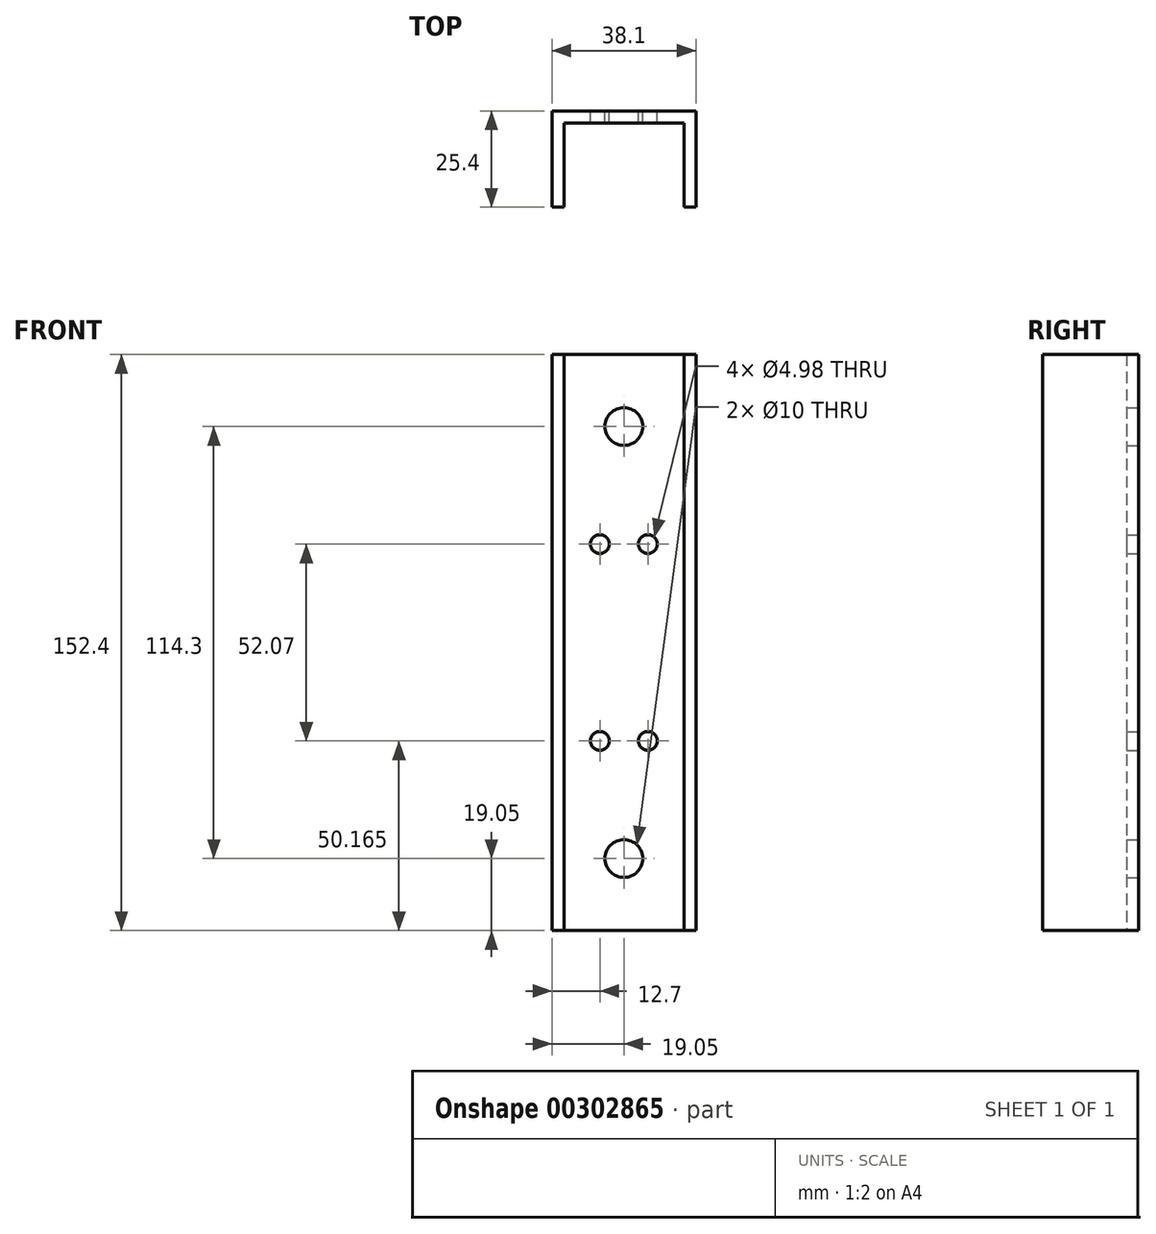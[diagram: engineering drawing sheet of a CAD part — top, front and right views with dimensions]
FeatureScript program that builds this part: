
annotation { "Feature Type Name" : "Feature", "Feature Type Description" : "" }
export const myFeature = defineFeature(function(context is Context, id is Id, definition is map)
    precondition{}
    {
        {
            var Q0;
            Q0=qCreatedBy(makeId("Top.planeOp"),FACE);
            var sketch = newSketch(context, id + "F0", { "sketchPlane" : qUnion([Q0])});
            skLineSegment(sketch, "E0", {"start": v(0, 0) * mm, "end": v(38.1, 0) * mm});
            skLineSegment(sketch, "E1", {"start": v(38.1, 0) * mm, "end": v(38.1, -25.4) * mm});
            skLineSegment(sketch, "E2", {"start": v(38.1, -25.4) * mm, "end": v(34.93, -25.4) * mm});
            skLineSegment(sketch, "E3", {"start": v(0, 0) * mm, "end": v(0, -25.4) * mm});
            skLineSegment(sketch, "E4", {"start": v(0, -25.4) * mm, "end": v(3.18, -25.4) * mm});
            skLineSegment(sketch, "E5", {"start": v(3.18, -25.4) * mm, "end": v(3.18, -3.18) * mm});
            skLineSegment(sketch, "E6", {"start": v(34.93, -25.4) * mm, "end": v(34.93, -3.18) * mm});
            skLineSegment(sketch, "E7", {"start": v(3.18, -3.18) * mm, "end": v(34.93, -3.18) * mm});
            skSolve(sketch);
        }
        {
            var Q0;
            Q0=makeQuery(id+"F0.imprint","IMPRINT",FACE,{"disambiguationData":[TD([[makeQuery(id+"F0.imprint","IMPRINT",EDGE,{"derivedFrom":sQuery(id+"F0.wireOp",EDGE,"E0")}),-1.0]])]});
            extrude(context, id + "F1", {"entities" : qUnion([Q0]), "depth" : 152.4 * mm});
        }
        {
            var Q0;
            Q0=makeQuery(id+"F1.opExtrude","SWEPT_FACE",FACE,{"disambiguationData":[OSD([sQuery(id+"F0.wireOp",EDGE,"E0")])]});
            var sketch = newSketch(context, id + "F2", { "sketchPlane" : qUnion([Q0])});
            skCircle(sketch, "E8", {"center": v(-19.05, 133.35) * mm, "radius": 5 * mm});
            skCircle(sketch, "E9", {"center": v(-19.05, 19.05) * mm, "radius": 5 * mm});
            skSolve(sketch);
        }
        {
            var Q0;
            Q0=qSketchRegion(id+"F2",true);
            extrude(context, id + "F3", {"entities" : qUnion([Q0]), "operationType" : NewBodyOperationType.REMOVE, "endBound" : BoundingType.THROUGH_ALL, "oppositeDirection" : true, "depth" : 25.4 * mm});
        }
        {
            var Q0;
            Q0=makeQuery(id+"F1.opExtrude","SWEPT_FACE",FACE,{"disambiguationData":[OSD([sQuery(id+"F0.wireOp",EDGE,"E0")])]});
            var sketch = newSketch(context, id + "F4", { "sketchPlane" : qUnion([Q0])});
            skCircle(sketch, "E10", {"center": v(-25.4, 102.24) * mm, "radius": 2.49 * mm});
            skCircle(sketch, "E11", {"center": v(-12.7, 102.24) * mm, "radius": 2.49 * mm});
            skCircle(sketch, "E12", {"center": v(-25.4, 50.17) * mm, "radius": 2.49 * mm});
            skCircle(sketch, "E13", {"center": v(-12.7, 50.17) * mm, "radius": 2.49 * mm});
            skLineSegment(sketch, "E14", {"start": v(0, 76.2) * mm, "end": v(-38.1, 76.2) * mm, "construction": true});
            skLineSegment(sketch, "E15", {"start": v(-38.1, 114.94) * mm, "end": v(0, 114.94) * mm, "construction": true});
            skCircle(sketch, "E16", {"center": v(-19.05, 133.35) * mm, "radius": 15.24 * mm, "construction": true});
            skSolve(sketch);
        }
        {
            var Q0;
            Q0=qSketchRegion(id+"F4",true);
            extrude(context, id + "F5", {"entities" : qUnion([Q0]), "operationType" : NewBodyOperationType.REMOVE, "endBound" : BoundingType.THROUGH_ALL, "oppositeDirection" : true, "depth" : 25.4 * mm});
        }
    });
